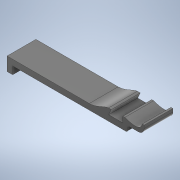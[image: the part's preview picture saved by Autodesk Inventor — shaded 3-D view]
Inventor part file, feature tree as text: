
AUTODESK INVENTOR PART (.ipt)
format: ipt  version: 2020 (Build 240168000, 168)  size: 220,160 bytes
history: native  units: mm
features: extrude x4, sketch x3, projected_geometry x2, other x1
ambient origin geometry x8: Origin, YZ Plane, XZ Plane, XY Plane, X Axis, Y Axis, Z Axis, Center Point
bodies: Body1 (feature_tree)
feature tree (10):
  other  "Твердое тело1"
  extrude  "Выдавливание1"  Depth=9.0mm
  extrude  "Выдавливание2"  Depth=3.0mm
  sketch  "Эскиз4"
  extrude  "Выдавливание3"  Depth=3.0mm
  extrude  "Выдавливание4"  Depth=2.5mm
  sketch  "Эскиз1"
  sketch  "Эскиз3"
  projected_geometry  "Спроецированная петля1"
  projected_geometry  "Спроецированная петля2"
